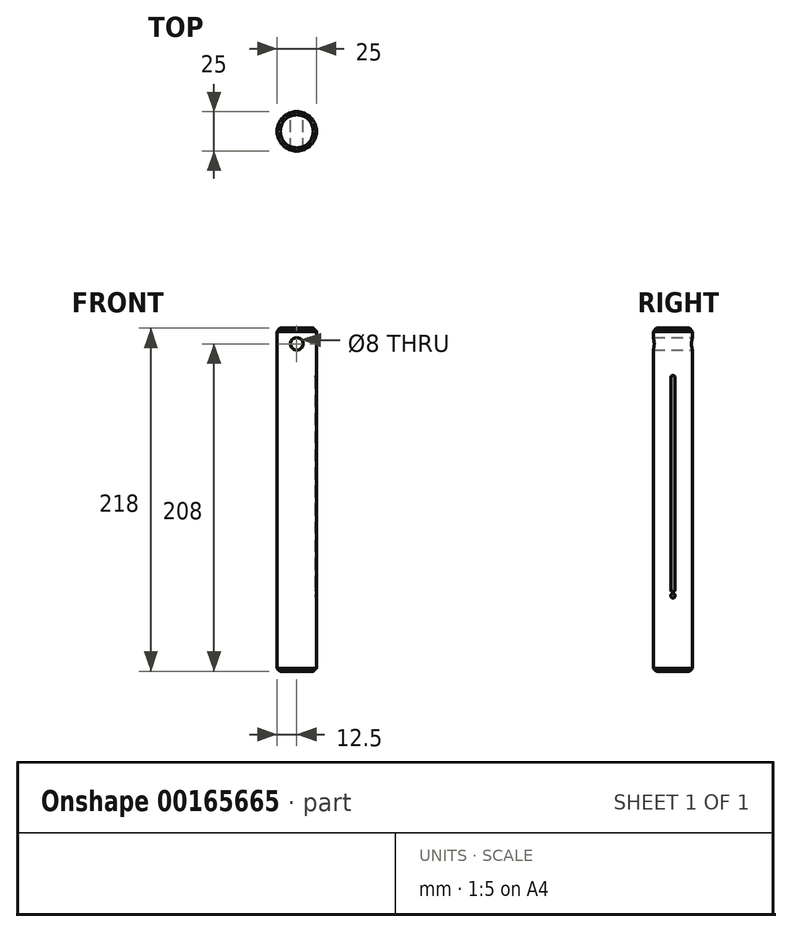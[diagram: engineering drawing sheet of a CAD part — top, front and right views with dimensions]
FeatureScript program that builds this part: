
annotation { "Feature Type Name" : "Feature", "Feature Type Description" : "" }
export const myFeature = defineFeature(function(context is Context, id is Id, definition is map)
    precondition{}
    {
        {
            var Q0;
            Q0=qCreatedBy(makeId("Top.planeOp"),FACE);
            var sketch = newSketch(context, id + "F0", { "sketchPlane" : qUnion([Q0])});
            skCircle(sketch, "E0", {"center": v(0, 0) * mm, "radius": 12.5 * mm});
            skSolve(sketch);
        }
        {
            var Q0;
            Q0=makeQuery(id+"F0.imprint","IMPRINT",FACE,{"disambiguationData":[TD([[makeQuery(id+"F0.imprint","IMPRINT",EDGE,{"derivedFrom":sQuery(id+"F0.wireOp",EDGE,"E0")}),1.0]])]});
            extrude(context, id + "F1", {"entities" : qUnion([Q0]), "depth" : 218 * mm, "offsetDistance" : 25 * mm});
        }
        {
            var Q0;
            Q0=makeQuery(id+"F1.opExtrude","CAP_EDGE",EDGE,{"disambiguationData":[OSD([sQuery(id+"F0.wireOp",EDGE,"E0")])],"isStart":true});
            var Q1;
            Q1=makeQuery(id+"F1.opExtrude","CAP_EDGE",EDGE,{"disambiguationData":[OSD([sQuery(id+"F0.wireOp",EDGE,"E0")])],"isStart":false});
            chamfer(context, id + "F2", {"entities" : qUnion([Q0, Q1]), "width" : 2 * mm, "tangentPropagation" : true});
        }
        {
            var Q0;
            Q0=qCreatedBy(makeId("Front.planeOp"),FACE);
            cPlane(context, id + "F3", {"entities" : qUnion([Q0]), "cplaneType" : CPlaneType.OFFSET, "offset" : 12.5 * mm, "oppositeDirection" : true, "width" : 150 * mm, "height" : 150 * mm});
        }
        {
            var Q0;
            Q0=qCreatedBy(id+"F3.planeOp",FACE);
            var sketch = newSketch(context, id + "F4", { "sketchPlane" : qUnion([Q0])});
            skCircle(sketch, "E1", {"center": v(0, 208) * mm, "radius": 4 * mm});
            skSolve(sketch);
        }
        {
            var Q0;
            Q0=makeQuery(id+"F4.imprint","IMPRINT",FACE,{"disambiguationData":[TD([[makeQuery(id+"F4.imprint","IMPRINT",EDGE,{"derivedFrom":sQuery(id+"F4.wireOp",EDGE,"E1")}),1.0]])]});
            var Q1;
            Q1=sQuery(id+"F4.wireOp",EDGE,"E1");
            extrude(context, id + "F5", {"entities" : qUnion([Q0]), "operationType" : NewBodyOperationType.REMOVE, "surfaceEntities" : qUnion([Q1]), "endBound" : BoundingType.THROUGH_ALL, "depth" : 25 * mm, "offsetDistance" : 25 * mm});
        }
        {
            var Q0;
            Q0=qCreatedBy(makeId("Top.planeOp"),FACE);
            cPlane(context, id + "F6", {"entities" : qUnion([Q0]), "cplaneType" : CPlaneType.OFFSET, "offset" : 52 * mm, "width" : 150 * mm, "height" : 150 * mm});
        }
        {
            var Q0;
            Q0=qCreatedBy(id+"F6.planeOp",FACE);
            var sketch = newSketch(context, id + "F7", { "sketchPlane" : qUnion([Q0]) });
            skLineSegment(sketch, "E2", {"start": v(13, 0) * mm, "end": v(13, 94.46) * mm, "construction": true});
            skArc(sketch, "E3", {"start": v(13, 1.5) * mm, "mid": v(11.5, 0) * mm, "end": v(13, -1.5) * mm});
            skLineSegment(sketch, "E4", {"start": v(13, 1.5) * mm, "end": v(13, -1.5) * mm});
            skSolve(sketch);
        }
        {
            var Q0;
            Q0=makeQuery(id+"F7.imprint","IMPRINT",FACE,{"disambiguationData":[TD([[makeQuery(id+"F7.imprint","IMPRINT",EDGE,{"derivedFrom":sQuery(id+"F7.wireOp",EDGE,"E3")}),1.0]])]});
            extrude(context, id + "F8", {"entities" : qUnion([Q0]), "operationType" : NewBodyOperationType.REMOVE, "depth" : 135 * mm, "offsetDistance" : 25 * mm});
        }
        {
            var Q0;
            Q0=qCreatedBy(id+"F6.planeOp",FACE);
            cPlane(context, id + "F9", {"entities" : qUnion([Q0]), "cplaneType" : CPlaneType.OFFSET, "offset" : 4 * mm, "oppositeDirection" : true, "width" : 150 * mm, "height" : 150 * mm});
        }
        {
            var Q0;
            Q0=qCreatedBy(id+"F9.planeOp",FACE);
            var sketch = newSketch(context, id + "F10", { "sketchPlane" : qUnion([Q0]) });
            skPoint(sketch, "E5.0", {"position": v(11.5, 0) * mm});
            skArc(sketch, "E6.0", {"start": v(13, 1.5) * mm, "mid": v(11.5, 0) * mm, "end": v(13, -1.5) * mm});
            skLineSegment(sketch, "E7.0", {"start": v(13, 1.5) * mm, "end": v(13, -1.5) * mm});
            skSolve(sketch);
        }
        {
            var Q0;
            Q0 = qSketchRegion(id + "F10", true);
            var Q1;
            Q1=sQuery(id+"F10.wireOp",EDGE,"E7.0");
            revolve(context, id + "F11", {"surfaceOperationType" : NewSurfaceOperationType.NEW, "entities" : qUnion([Q0]), "axis" : qUnion([Q1]), "revolveType" : RevolveType.FULL});
        }
        {
            var Q0;
            Q0=makeQuery(id+"F11.opRevolve","SWEPT_BODY",BODY,{"disambiguationData":[OSD([sQuery(id+"F10.wireOp",EDGE,"E6.0"),sQuery(id+"F10.wireOp",EDGE,"E7.0")])]});
            var Q1;
            Q1=makeQuery(id+"F1.opExtrude","SWEPT_BODY",BODY,{"disambiguationData":[OSD([sQuery(id+"F0.wireOp",EDGE,"E0")])]});
            booleanBodies(context, id + "F12", {"operationType" : BooleanOperationType.SUBTRACTION, "tools" : qUnion([Q0]), "targets" : qUnion([Q1])});
        }
        {
            var Q0;
            Q0=makeQuery(id+"F7.imprint","IMPRINT",FACE,{"disambiguationData":[TD([[makeQuery(id+"F7.imprint","IMPRINT",EDGE,{"derivedFrom":sQuery(id+"F7.wireOp",EDGE,"E3")}),1.0]])]});
            var Q1;
            Q1=sQuery(id+"F7.wireOp",EDGE,"E4");
            revolve(context, id + "F13", {"operationType" : NewBodyOperationType.REMOVE, "surfaceOperationType" : NewSurfaceOperationType.NEW, "entities" : qUnion([Q0]), "axis" : qUnion([Q1]), "revolveType" : RevolveType.FULL, "oppositeDirection" : true});
        }
        {
            var Q0;
            Q0=makeQuery(id+"F8.boolean.opBoolean","COPY",FACE,{"derivedFrom":makeQuery(id+"F8.opExtrude","CAP_FACE",FACE,{"disambiguationData":[OSD([sQuery(id+"F7.wireOp",EDGE,"E3"),sQuery(id+"F7.wireOp",EDGE,"E4")])],"isStart":false})});
            var sketch = newSketch(context, id + "F14", { "sketchPlane" : qUnion([Q0]) });
            skArc(sketch, "E8.0", {"start": v(12.42, -1.38) * mm, "mid": v(11.5, 0) * mm, "end": v(12.42, 1.38) * mm});
            skLineSegment(sketch, "E9", {"start": v(12.42, 1.38) * mm, "end": v(12.42, -1.38) * mm});
            skSolve(sketch);
        }
        {
            var Q0;
            Q0 = qSketchRegion(id + "F14", true);
            var Q1;
            Q1=sQuery(id+"F14.wireOp",EDGE,"E9");
            revolve(context, id + "F15", {"operationType" : NewBodyOperationType.REMOVE, "surfaceOperationType" : NewSurfaceOperationType.NEW, "entities" : qUnion([Q0]), "axis" : qUnion([Q1]), "revolveType" : RevolveType.FULL, "oppositeDirection" : true});
        }
    });
